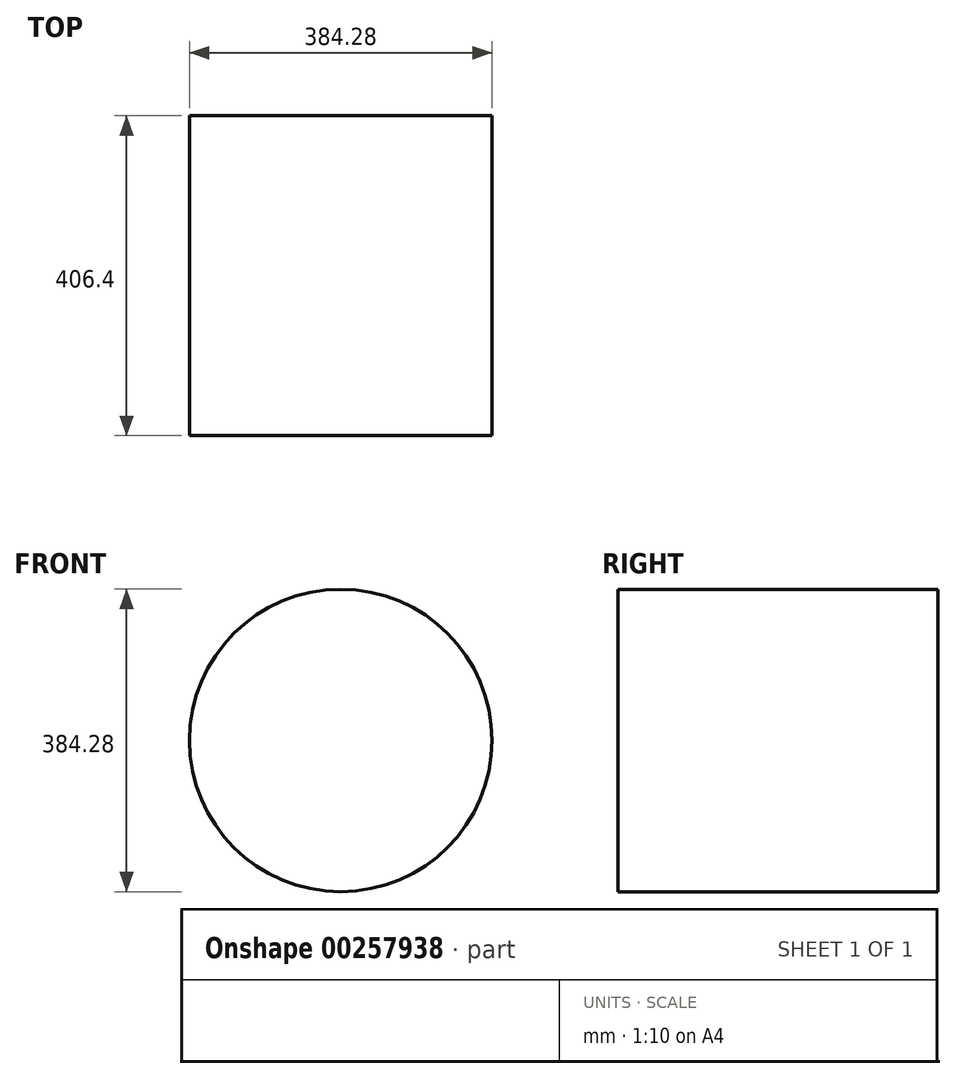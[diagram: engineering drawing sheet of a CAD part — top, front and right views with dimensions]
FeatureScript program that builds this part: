
annotation { "Feature Type Name" : "Feature", "Feature Type Description" : "" }
export const myFeature = defineFeature(function(context is Context, id is Id, definition is map)
    precondition{}
    {
        {
            var Q0;
            Q0=qCreatedBy(makeId("Front.planeOp"),FACE);
            var sketch = newSketch(context, id + "F0", { "sketchPlane" : qUnion([Q0])});
            skCircle(sketch, "E0", {"center": v(0, 0) * mm, "radius": 192.14 * mm});
            skSolve(sketch);
        }
        {
            var Q0;
            Q0=makeQuery(id+"F0.imprint","IMPRINT",FACE,{"disambiguationData":[TD([[makeQuery(id+"F0.imprint","IMPRINT",EDGE,{"derivedFrom":sQuery(id+"F0.wireOp",EDGE,"E0")}),1.0]])]});
            extrude(context, id + "F1", {"entities" : qUnion([Q0]), "depth" : 203.2 * mm, "hasSecondDirection" : true, "secondDirectionOppositeDirection" : true, "secondDirectionDepth" : 203.2 * mm});
        }
    });
